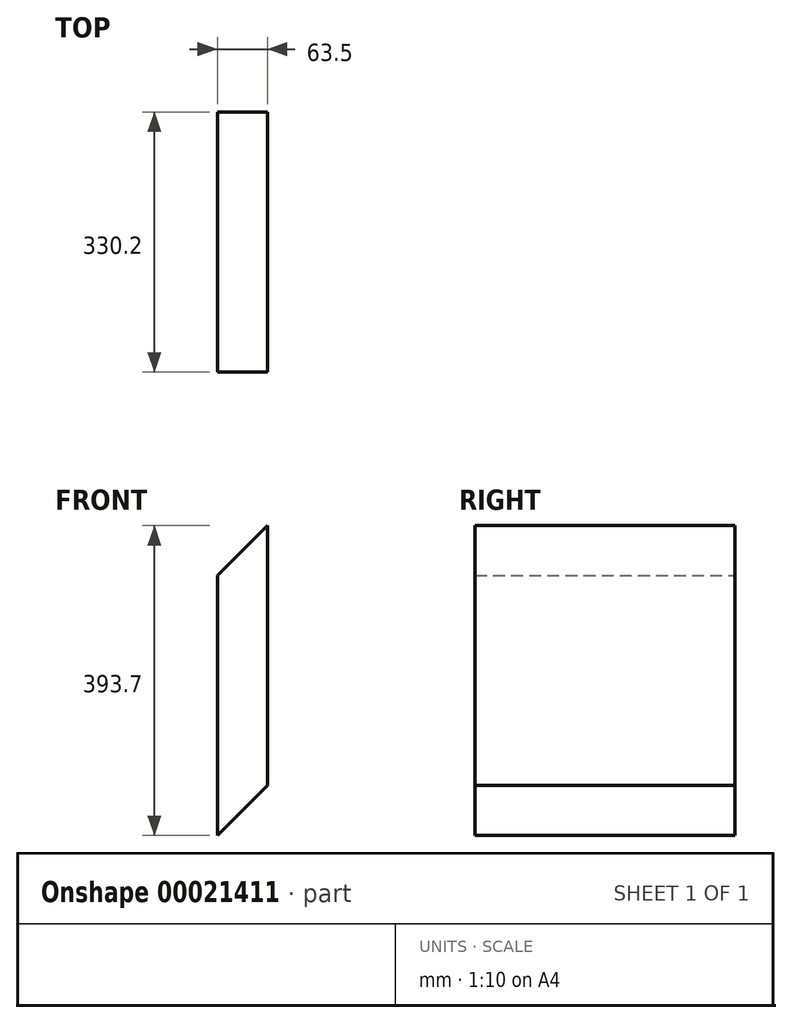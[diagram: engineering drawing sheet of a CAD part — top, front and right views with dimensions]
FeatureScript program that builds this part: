
annotation { "Feature Type Name" : "Feature", "Feature Type Description" : "" }
export const myFeature = defineFeature(function(context is Context, id is Id, definition is map)
    precondition{}
    {
        {
            var Q0;
            Q0=qCreatedBy(makeId("Front.planeOp"),FACE);
            var sketch = newSketch(context, id + "F0", { "sketchPlane" : qUnion([Q0])});
            skLineSegment(sketch, "E0", {"start": v(0, 0) * mm, "end": v(0, 330.2) * mm});
            skLineSegment(sketch, "E1", {"start": v(0, 330.2) * mm, "end": v(63.5, 393.7) * mm});
            skLineSegment(sketch, "E2", {"start": v(63.5, 393.7) * mm, "end": v(63.5, 63.5) * mm});
            skLineSegment(sketch, "E3", {"start": v(63.5, 63.5) * mm, "end": v(0, 0) * mm});
            skSolve(sketch);
        }
        {
            var Q0;
            Q0=makeQuery(id+"F0.imprint","IMPRINT",FACE,{"disambiguationData":[TD([[makeQuery(id+"F0.imprint","IMPRINT",EDGE,{"derivedFrom":sQuery(id+"F0.wireOp",EDGE,"E0")}),-1.0]])]});
            extrude(context, id + "F1", {"entities" : qUnion([Q0]), "depth" : 330.2 * mm});
        }
    });
